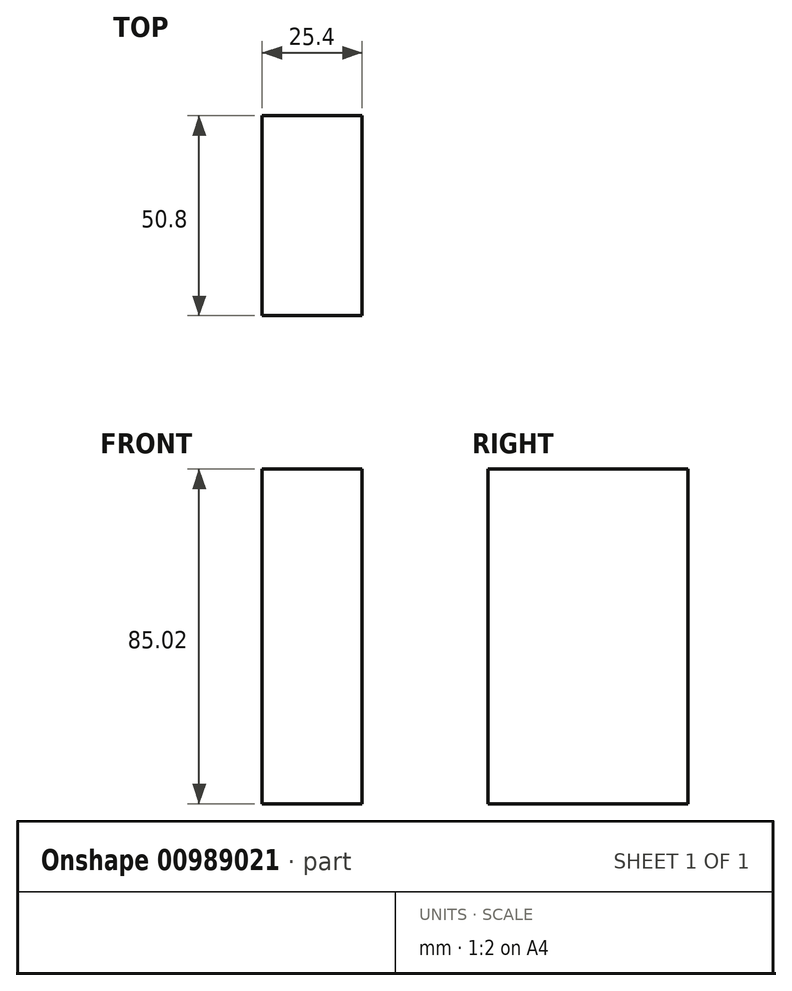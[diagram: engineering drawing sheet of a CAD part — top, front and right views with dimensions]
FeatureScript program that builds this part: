
annotation { "Feature Type Name" : "Feature", "Feature Type Description" : "" }
export const myFeature = defineFeature(function(context is Context, id is Id, definition is map)
    precondition{}
    {
        {
            var Q0;
            Q0=qCreatedBy(makeId("Right.planeOp"),FACE);
            var sketch = newSketch(context, id + "F0", { "sketchPlane" : qUnion([Q0])});
            skLineSegment(sketch, "E0.bottom", {"start": v(-89.43, 0) * mm, "end": v(-39.91, 0) * mm});
            skLineSegment(sketch, "E0.top", {"start": v(-89.43, -85.02) * mm, "end": v(-39.91, -85.02) * mm});
            skLineSegment(sketch, "E0.left", {"start": v(-89.43, 0) * mm, "end": v(-89.43, -85.02) * mm});
            skLineSegment(sketch, "E0.right", {"start": v(-39.91, 0) * mm, "end": v(-39.91, -85.02) * mm});
            skSolve(sketch);
        }
        {
            var Q0;
            Q0=sQuery(id+"F0.wireOp",EDGE,"E0.right");
            extrude(context, id + "F1", {"bodyType" : ToolBodyType.SURFACE, "surfaceEntities" : qUnion([Q0]), "depth" : 25.4 * mm, "offsetDistance" : 25.4 * mm});
        }
        {
            var Q0;
            Q0=makeQuery(id+"F1.opExtrude","SWEPT_FACE",FACE,{"disambiguationData":[OSD([sQuery(id+"F0.wireOp",EDGE,"E0.right")])]});
            extrude(context, id + "F2", {"entities" : qUnion([Q0]), "depth" : 50.8 * mm, "offsetDistance" : 25.4 * mm});
        }
    });
